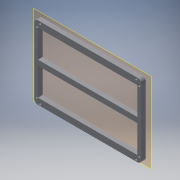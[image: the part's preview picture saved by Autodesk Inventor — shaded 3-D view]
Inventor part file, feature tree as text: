
AUTODESK INVENTOR PART (.ipt)
format: ipt  version: 2019.4 (Build 234330000, 330)  size: 138,240 bytes
history: native  units: mm
features: other x5, reference x3, plane x2, sketch x1, extrude x1
ambient origin geometry x8: Origin, YZ Plane, XZ Plane, XY Plane, X Axis, Y Axis, Z Axis, Center Point
bodies: Solid1 (feature_tree)
feature tree (12):
  plane  "Work Plane1"
  sketch  "Sketch1"  dims[d0=0.2mm d1=0.2mm d2=0.2mm d3=0.2mm d4=10.0mm d5=0.0mm]
  plane  "Work Plane2"
  extrude  "Extrusion1"  Depth=10.0mm
  reference  "Reference1"
  reference  "Reference2"
  reference  "Reference3"
  other  "Full_HITscope_v0.iam"
  other  "05_Omniscope_base_v1:1"
  other  "Assembly_Omniscope_v1:12"
  other  "Omnivision_Objectivelens_mount:1"
  other  "Assembly_Omniscope_v1:11"
